# Revit family: M_Downlight - Spot
name_source: partatom
category: Lighting Fixtures
revit_build: Autodesk Revit 2017 (Build: 20160109_1515(x64)
units: mm (PartAtom-declared; Revit-internal decimal feet)

## family parameters
Always vertical = No
Cut with Voids When Loaded = No
Host = Ceiling
Light Source = Yes
OmniClass Number = 23.80.70.11.14.11
OmniClass Title = Downlights
Part Type = Normal
Room Calculation Point = No
Round Connector Dimension = Use Diameter
Shared = No

## types (6) — shared parameters
Apparent Load = 40 VA
Assembly Code = D5020230
Ballast Number of Poles = 1
Color Filter = 16777215
Diffuser = Glass, White, High Luminance
Dimming Lamp Color Temperature Shift = <None>
Lamp Half Width = 50 mm  [stored 0.164042 ft]
Lamp Height = 75 mm
Lamp Width = 100 mm  [stored 0.328084 ft]
Light Casing Material = Plastic, Opaque Black
Load Classification = Lighting - Dwelling Unit
Spot Beam Angle = 30.00°
Spot Field Angle = 90.00°
Wattage Comments = 40

## per-type parameters (varying)
| type | Ballast Voltage | Light Source Symbol Length | Tilt Angle |
| 90 Degree Tilt - 277V | 277 V | 3048 mm  [stored 10 ft] | 90.00° |
| 75 Degree Tilt - 277V | 277 V | 3048 mm  [stored 10 ft] | 75.00° |
| 60 Degree Tilt - 120V | 120 V | 3048 mm  [stored 10 ft] | 60.00° |
| 60 Degree Tilt - 277V | 277 V | 3048 mm  [stored 10 ft] | 60.00° |
| 75 Degree Tilt - 120V | 120 V | 600 mm | 75.00° |
| 90 Degree Tilt - 120V | 120 V | 3048 mm  [stored 10 ft] | 90.00° |

note: [stored X ft] marks values corroborated as IEEE doubles in the binary element streams (Revit-internal decimal feet)

## geometry (parser evidence)
native form markers: Sweep x1
no freeform markers — native parametric forms only
